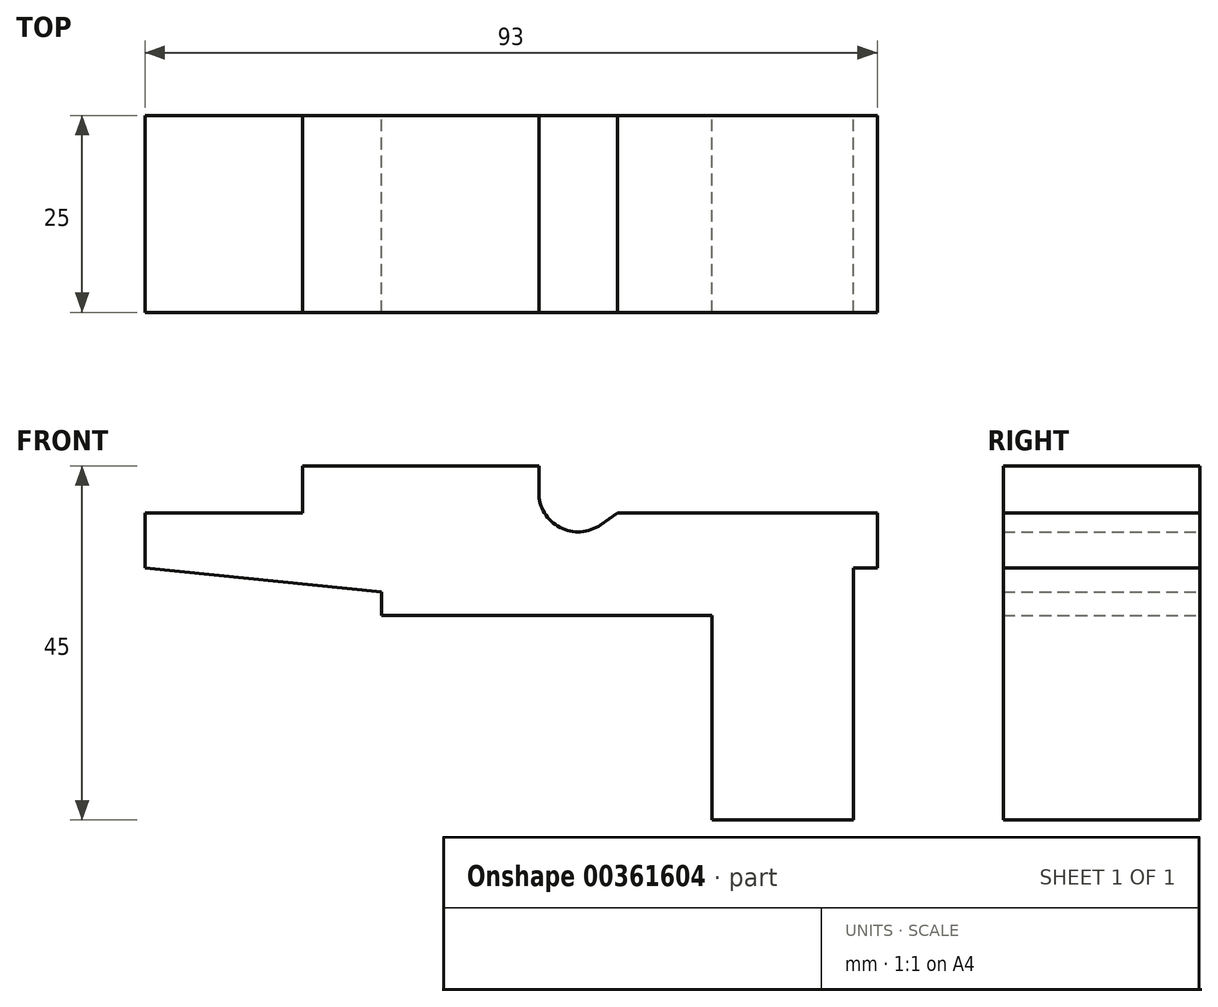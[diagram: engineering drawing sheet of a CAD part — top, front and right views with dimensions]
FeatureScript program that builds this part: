
annotation { "Feature Type Name" : "Feature", "Feature Type Description" : "" }
export const myFeature = defineFeature(function(context is Context, id is Id, definition is map)
    precondition{}
    {
        {
            var Q0;
            Q0=qCreatedBy(makeId("Front.planeOp"),FACE);
            var sketch = newSketch(context, id + "F0", { "sketchPlane" : qUnion([Q0])});
            skLineSegment(sketch, "E0", {"start": v(-42, 0) * mm, "end": v(0, 0) * mm});
            skLineSegment(sketch, "E1", {"start": v(0, 0) * mm, "end": v(0, -26) * mm});
            skLineSegment(sketch, "E2", {"start": v(0, -26) * mm, "end": v(18, -26) * mm});
            skLineSegment(sketch, "E3", {"start": v(18, -26) * mm, "end": v(18, 6) * mm});
            skLineSegment(sketch, "E4", {"start": v(18, 6) * mm, "end": v(21, 6) * mm});
            skLineSegment(sketch, "E5", {"start": v(21, 6) * mm, "end": v(21, 13) * mm});
            skLineSegment(sketch, "E6", {"start": v(21, 13) * mm, "end": v(-12, 13) * mm});
            skLineSegment(sketch, "E7", {"start": v(-12, 13) * mm, "end": v(-14.13, 11.5) * mm});
            skLineSegment(sketch, "E8", {"start": v(-52, 13) * mm, "end": v(-72, 13) * mm});
            skLineSegment(sketch, "E9", {"start": v(-72, 13) * mm, "end": v(-72, 6) * mm});
            skLineSegment(sketch, "E10", {"start": v(-72, 6) * mm, "end": v(-42, 3) * mm});
            skLineSegment(sketch, "E11", {"start": v(-42, 3) * mm, "end": v(-42, 0) * mm});
            skLineSegment(sketch, "E12", {"start": v(-22, 15.6) * mm, "end": v(-22, 19) * mm});
            skLineSegment(sketch, "E13", {"start": v(-22, 19) * mm, "end": v(-52, 19) * mm});
            skLineSegment(sketch, "E14", {"start": v(-52, 19) * mm, "end": v(-52, 13) * mm});
            skPoint(sketch, "E15.visualSharp", {"position": v(-22, 6) * mm});
            skArc(sketch, "E15.filletArc", {"start": v(-22, 15.6) * mm, "mid": v(-19.3, 11.17) * mm, "end": v(-14.13, 11.5) * mm});
            skSolve(sketch);
        }
        {
            var Q0;
            Q0=makeQuery(id+"F0.imprint","IMPRINT",FACE,{"disambiguationData":[TD([[makeQuery(id+"F0.imprint","IMPRINT",EDGE,{"derivedFrom":sQuery(id+"F0.wireOp",EDGE,"E0")}),1.0]])]});
            extrude(context, id + "F1", {"entities" : qUnion([Q0]), "depth" : 25 * mm});
        }
    });
